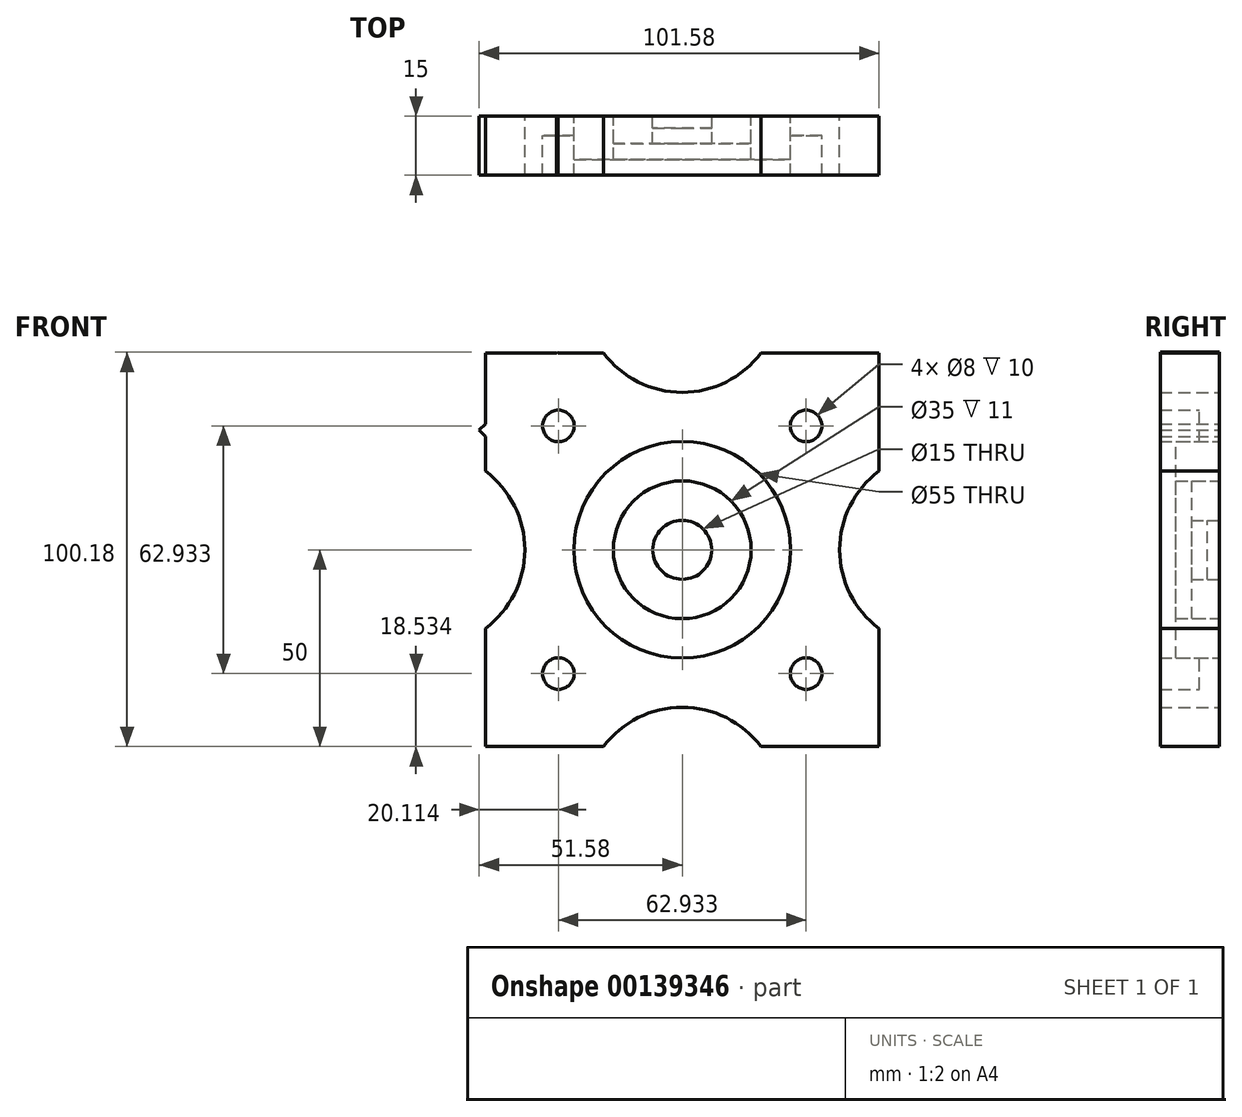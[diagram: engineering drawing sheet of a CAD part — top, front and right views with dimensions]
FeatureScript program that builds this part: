
annotation { "Feature Type Name" : "Feature", "Feature Type Description" : "" }
export const myFeature = defineFeature(function(context is Context, id is Id, definition is map)
    precondition{}
    {
        {
            var Q0;
            Q0=qCreatedBy(makeId("Front.planeOp"),FACE);
            var sketch = newSketch(context, id + "F0", { "sketchPlane" : qUnion([Q0])});
            skCircle(sketch, "E0", {"center": v(0, 0) * mm, "radius": 7.5 * mm});
            skCircle(sketch, "E1", {"center": v(0, 0) * mm, "radius": 17.5 * mm});
            skCircle(sketch, "E2", {"center": v(0, 0) * mm, "radius": 27.5 * mm});
            skLineSegment(sketch, "E3", {"start": v(-50, 50) * mm, "end": v(-50, 20) * mm});
            skLineSegment(sketch, "E4", {"start": v(-50, -50) * mm, "end": v(-50, -20) * mm});
            skArc(sketch, "E5", {"start": v(-50, -20) * mm, "mid": v(-40, 0) * mm, "end": v(-50, 20) * mm});
            skLineSegment(sketch, "E6", {"start": v(-50, 50) * mm, "end": v(-20, 50) * mm});
            skLineSegment(sketch, "E7", {"start": v(50, 50) * mm, "end": v(20, 50) * mm});
            skLineSegment(sketch, "E8", {"start": v(50, 50) * mm, "end": v(50, 20) * mm});
            skLineSegment(sketch, "E9", {"start": v(50, -50) * mm, "end": v(50, -20) * mm});
            skLineSegment(sketch, "E10", {"start": v(50, -50) * mm, "end": v(20, -50) * mm});
            skLineSegment(sketch, "E11", {"start": v(-50, -50) * mm, "end": v(-20, -50) * mm});
            skArc(sketch, "E12", {"start": v(-20, 50) * mm, "mid": v(0, 40) * mm, "end": v(20, 50) * mm});
            skArc(sketch, "E13", {"start": v(50, 20) * mm, "mid": v(40, 0) * mm, "end": v(50, -20) * mm});
            skArc(sketch, "E14", {"start": v(20, -50) * mm, "mid": v(0, -40) * mm, "end": v(-20, -50) * mm});
            skCircle(sketch, "E15", {"center": v(-31.47, 31.47) * mm, "radius": 4 * mm});
            skCircle(sketch, "E16", {"center": v(31.47, 31.47) * mm, "radius": 4 * mm});
            skCircle(sketch, "E17", {"center": v(31.47, -31.47) * mm, "radius": 4 * mm});
            skCircle(sketch, "E18", {"center": v(-31.47, -31.47) * mm, "radius": 4 * mm});
            skLineSegment(sketch, "E19", {"start": v(-50, 50) * mm, "end": v(50, -50) * mm, "construction": true});
            skLineSegment(sketch, "E20.0", {"start": v(-51.58, 30.38) * mm, "end": v(-31.78, 50.18) * mm});
            skLineSegment(sketch, "E20.1", {"start": v(-31.78, 50.18) * mm, "end": v(-15.9, 34.3) * mm});
            skLineSegment(sketch, "E20.2", {"start": v(-15.9, 34.3) * mm, "end": v(-35.7, 14.5) * mm});
            skLineSegment(sketch, "E20.3", {"start": v(-35.7, 14.5) * mm, "end": v(-51.58, 30.38) * mm});
            skPoint(sketch, "E20.0.midPoint", {"position": v(-41.68, 40.28) * mm});
            skSolve(sketch);
        }
        {
            var Q0;
            Q0 = qSketchRegion(id + "F0", true);
            extrude(context, id + "F1", {"entities" : qUnion([Q0]), "depth" : 15 * mm});
        }
        {
            var Q0;
            Q0=makeQuery(id+"F0.imprint","IMPRINT",FACE,{"disambiguationData":[TD([[makeQuery(id+"F0.imprint","IMPRINT",EDGE,{"derivedFrom":sQuery(id+"F0.wireOp",EDGE,"E1")}),-1.0]])]});
            extrude(context, id + "F2", {"entities" : qUnion([Q0]), "depth" : 11 * mm});
        }
        {
            var Q0;
            Q0=makeQuery(id+"F0.imprint","IMPRINT",FACE,{"disambiguationData":[TD([[makeQuery(id+"F0.imprint","IMPRINT",EDGE,{"derivedFrom":sQuery(id+"F0.wireOp",EDGE,"E0")}),-1.0]])]});
            extrude(context, id + "F3", {"entities" : qUnion([Q0]), "depth" : 7 * mm});
        }
        {
            var Q0;
            Q0=makeQuery(id+"F0.imprint","IMPRINT",FACE,{"disambiguationData":[TD([[makeQuery(id+"F0.imprint","IMPRINT",EDGE,{"derivedFrom":sQuery(id+"F0.wireOp",EDGE,"E0")}),1.0]])]});
            extrude(context, id + "F4", {"entities" : qUnion([Q0]), "depth" : 3 * mm});
        }
        {
            var Q0;
            Q0=makeQuery(id+"F0.imprint","IMPRINT",FACE,{"disambiguationData":[TD([[makeQuery(id+"F0.imprint","IMPRINT",EDGE,{"derivedFrom":sQuery(id+"F0.wireOp",EDGE,"E15")}),1.0]])]});
            var Q1;
            Q1=makeQuery(id+"F0.imprint","IMPRINT",FACE,{"disambiguationData":[TD([[makeQuery(id+"F0.imprint","IMPRINT",EDGE,{"derivedFrom":sQuery(id+"F0.wireOp",EDGE,"E16")}),1.0]])]});
            var Q2;
            Q2=makeQuery(id+"F0.imprint","IMPRINT",FACE,{"disambiguationData":[TD([[makeQuery(id+"F0.imprint","IMPRINT",EDGE,{"derivedFrom":sQuery(id+"F0.wireOp",EDGE,"E17")}),1.0]])]});
            var Q3;
            Q3=makeQuery(id+"F0.imprint","IMPRINT",FACE,{"disambiguationData":[TD([[makeQuery(id+"F0.imprint","IMPRINT",EDGE,{"derivedFrom":sQuery(id+"F0.wireOp",EDGE,"E18")}),1.0]])]});
            extrude(context, id + "F5", {"entities" : qUnion([Q0, Q1, Q2, Q3]), "operationType" : NewBodyOperationType.ADD, "depth" : 5 * mm});
        }
    });
